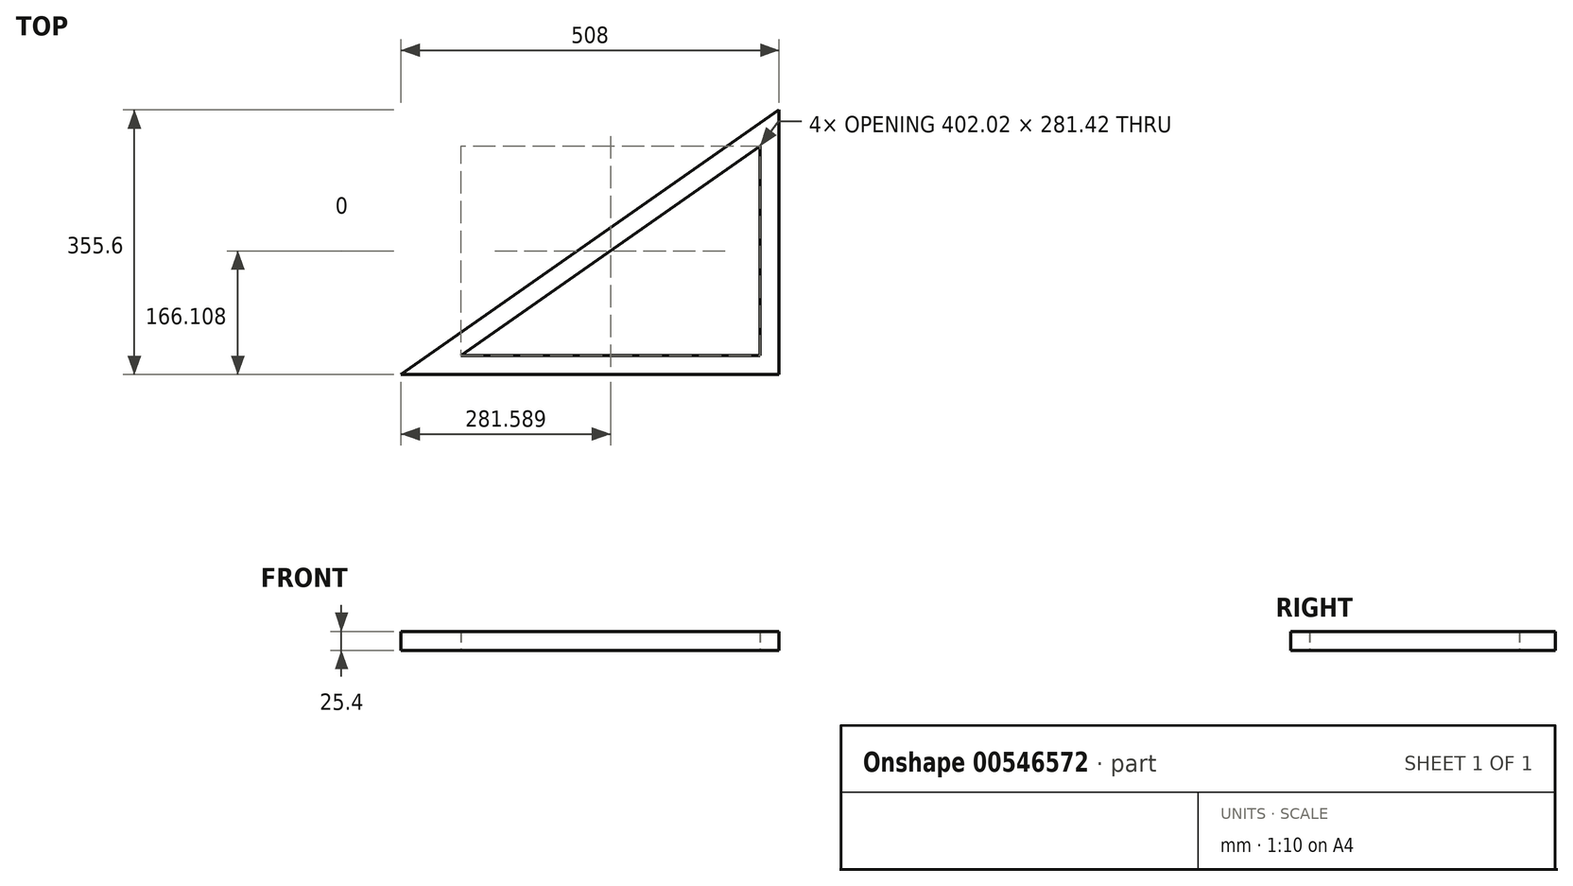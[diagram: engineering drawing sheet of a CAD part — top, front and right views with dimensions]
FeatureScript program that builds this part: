
annotation { "Feature Type Name" : "Feature", "Feature Type Description" : "" }
export const myFeature = defineFeature(function(context is Context, id is Id, definition is map)
    precondition{}
    {
        {
            var Q0;
            Q0=qCreatedBy(makeId("Top.planeOp"),FACE);
            var sketch = newSketch(context, id + "F0", { "sketchPlane" : qUnion([Q0])});
            skLineSegment(sketch, "E0", {"start": v(0, 0) * mm, "end": v(0, 355.6) * mm});
            skLineSegment(sketch, "E1", {"start": v(0, 355.6) * mm, "end": v(-508, 0) * mm});
            skLineSegment(sketch, "E2", {"start": v(-508, 0) * mm, "end": v(0, 0) * mm});
            skLineSegment(sketch, "E3.0", {"start": v(-25.4, 306.82) * mm, "end": v(-427.42, 25.4) * mm});
            skLineSegment(sketch, "E3.1", {"start": v(-25.4, 25.4) * mm, "end": v(-25.4, 306.82) * mm});
            skLineSegment(sketch, "E3.2", {"start": v(-427.42, 25.4) * mm, "end": v(-25.4, 25.4) * mm});
            skSolve(sketch);
        }
        {
            var Q0;
            Q0=makeQuery(id+"F0.imprint","IMPRINT",FACE,{"disambiguationData":[TD([[makeQuery(id+"F0.imprint","IMPRINT",EDGE,{"derivedFrom":sQuery(id+"F0.wireOp",EDGE,"E0")}),1.0]])]});
            extrude(context, id + "F1", {"entities" : qUnion([Q0]), "depth" : 25.4 * mm, "offsetDistance" : 25.4 * mm});
        }
    });
